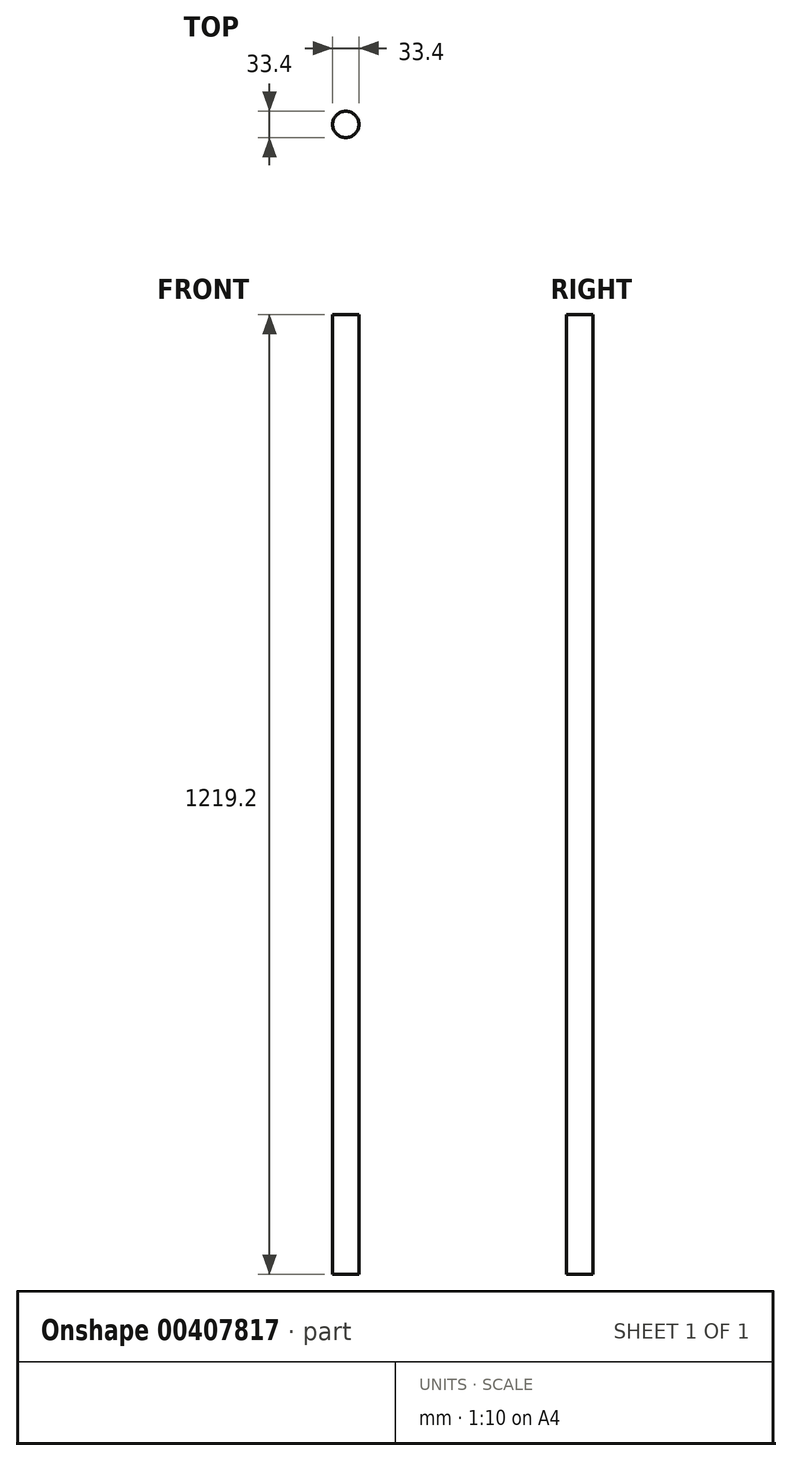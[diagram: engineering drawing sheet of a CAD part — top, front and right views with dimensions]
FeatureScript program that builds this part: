
annotation { "Feature Type Name" : "Feature", "Feature Type Description" : "" }
export const myFeature = defineFeature(function(context is Context, id is Id, definition is map)
    precondition{}
    {
        {
            var Q0;
            Q0=qCreatedBy(makeId("Top.planeOp"),FACE);
            var sketch = newSketch(context, id + "F0", { "sketchPlane" : qUnion([Q0])});
            skCircle(sketch, "E0", {"center": v(0, 0) * mm, "radius": 16.7 * mm});
            skSolve(sketch);
        }
        {
            var Q0;
            Q0 = qSketchRegion(id + "F0", true);
            extrude(context, id + "F1", {"entities" : qUnion([Q0]), "depth" : 1219.2 * mm});
        }
    });
